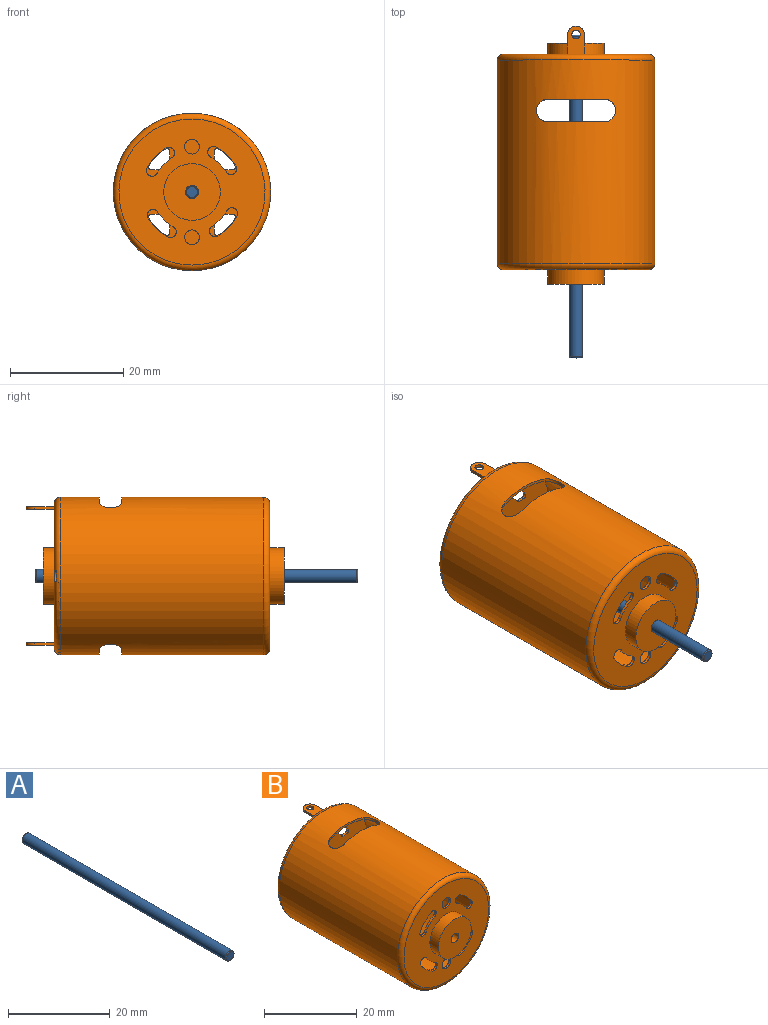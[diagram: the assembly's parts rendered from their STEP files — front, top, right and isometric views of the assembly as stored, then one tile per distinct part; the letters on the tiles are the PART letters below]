
ASSEMBLY  parts=2 mates=1
PART A: 5 faces, bbox 2.5x57x2.5 mm
  f0: cylinder r=1.15mm len=56.6mm, axis (0,1,0), area 409mm2, adj f3,f4
  f1: plane 1.9x1.9mm, normal (0,-1,0), area 2.8mm2, adj f4
  f2: plane 1.9x1.9mm, normal (0,1,0), area 2.8mm2, adj f3
  f3: torus R=0.95mm, axis (0,-1,0), area 2.1mm2, adj f0,f2
  f4: torus R=0.95mm, axis (0,-1,0), area 2.1mm2, adj f0,f1
PART B: 92 faces, bbox 30.1x45.6x30.1 mm
  f0: plane 25.8x25.72mm, normal (0,1,0), area 404mm2, adj f12,f22,f23,f24,f26,f27,f28,f30
  f1: plane 25.8x25.8mm, normal (0,-1,0), area 386.1mm2, adj f4,f5,f10,f62,f63,f64,f65,f66
  f2: plane 26.8x26.8mm, normal (0,1,0), area 501.8mm2, adj f4,f5,f7,f9,f62,f63,f64,f65
  f3: cylinder r=13.9mm len=36mm, axis (0,-1,0), area 3034.5mm2, adj f14,f15,f16,f17,f18,f19,f20,f21
  f4: cylinder r=1.3mm len=2.6mm, axis (0,-1,0), area 4.1mm2, adj f1,f2
  f5: cylinder r=1.3mm len=2.6mm, axis (0,-1,0), area 4.1mm2, adj f1,f2
  f6: plane 26.8x26.8mm, normal (0,-1,0), area 527.4mm2, adj f7,f8,f30,f31,f32,f33,f34,f35
  f7: cylinder r=13.4mm len=37mm, axis (0,-1,0), area 3005.2mm2, adj f2,f6,f14,f15,f16,f17,f18,f19
  f8: cylinder r=1.15mm len=2.5mm, axis (0,-1,0), area 18.1mm2, adj f6,f13
  f9: cylinder r=1.15mm len=3.1mm, axis (0,-1,0), area 22.4mm2, adj f2,f11
  f10: cylinder r=5mm len=10mm, axis (0,1,0), area 81.7mm2, adj f1,f11
  f11: plane 10x10mm, normal (0,-1,0), area 74.4mm2, adj f9,f10
  f12: cylinder r=5mm len=10mm, axis (0,-1,0), area 62.8mm2, adj f0,f13
  f13: plane 10x10mm, normal (0,1,0), area 74.4mm2, adj f8,f12
  f14: plane 10x1.47mm, normal (0,1,0), area 5.1mm2, adj f3,f7,f15,f17
  f15: cylinder r=2mm len=4mm, axis (0,0,1), area 3.5mm2, adj f3,f7,f14,f16
  f16: plane 10x1.47mm, normal (0,-1,0), area 5.1mm2, adj f3,f7,f15,f17
  f17: cylinder r=2mm len=4mm, axis (0,0,1), area 3.5mm2, adj f3,f7,f14,f16
  f18: cylinder r=2mm len=4mm, axis (0,0,1), area 3.5mm2, adj f3,f7,f19,f21
  f19: plane 10x1.47mm, normal (0,-1,0), area 5.1mm2, adj f3,f7,f18,f20
  f20: cylinder r=2mm len=4mm, axis (0,0,1), area 3.5mm2, adj f3,f7,f19,f21
  f21: plane 10x1.47mm, normal (0,1,0), area 5.1mm2, adj f3,f7,f18,f20
  f22: cylinder r=1mm len=2mm, axis (0,1,0), area 0.9mm2, adj f0,f23,f24,f25
  f23: plane 1.08x0.31mm, normal (0,0,-1), area 0.3mm2, adj f0,f22,f25,f79
  f24: plane 1.08x0.31mm, normal (0,0,1), area 0.3mm2, adj f0,f22,f25,f79
  f25: plane 2.11x2mm, normal (0,1,0), area 3.8mm2, adj f22,f23,f24,f79
  f26: plane 1.08x0.31mm, normal (0,0,-1), area 0.3mm2, adj f0,f27,f29,f79
  f27: cylinder r=1mm len=2mm, axis (0,1,0), area 0.9mm2, adj f0,f26,f28,f29
  f28: plane 1.08x0.31mm, normal (0,0,1), area 0.3mm2, adj f0,f27,f29,f79
  f29: plane 2.11x2mm, normal (0,1,0), area 3.8mm2, adj f26,f27,f28,f79
  f30: cylinder r=8.9mm len=2.92mm, axis (0,1,0), area 2.1mm2, adj f0,f6,f34,f35
  f31: plane 1.21x0.5mm, normal (1,0,0), area 0.6mm2, adj f0,f6,f34,f36
  f32: plane 1.21x0.5mm, normal (0,0,1), area 0.6mm2, adj f0,f6,f35,f37
  f33: cylinder r=6.9mm len=1.45mm, axis (0,1,0), area 1mm2, adj f0,f6,f36,f37
  f34: cylinder r=0.5mm len=0.76mm, axis (0,1,0), area 0.5mm2, adj f0,f6,f30,f31
  f35: cylinder r=0.5mm len=0.76mm, axis (0,1,0), area 0.5mm2, adj f0,f6,f30,f32
  f36: cylinder r=0.5mm len=0.5mm, axis (0,1,0), area 0.2mm2, adj f0,f6,f31,f33
  f37: cylinder r=0.5mm len=0.5mm, axis (0,1,0), area 0.2mm2, adj f0,f6,f32,f33
  f38: cylinder r=8.9mm len=2.92mm, axis (0,1,0), area 2.1mm2, adj f0,f6,f42,f43
  f39: plane 1.21x0.5mm, normal (0,0,-1), area 0.6mm2, adj f0,f6,f42,f44
  f40: plane 1.21x0.5mm, normal (1,0,0), area 0.6mm2, adj f0,f6,f43,f45
  f41: cylinder r=6.9mm len=1.45mm, axis (0,1,0), area 1mm2, adj f0,f6,f44,f45
  f42: cylinder r=0.5mm len=0.76mm, axis (0,1,0), area 0.5mm2, adj f0,f6,f38,f39
  f43: cylinder r=0.5mm len=0.76mm, axis (0,1,0), area 0.5mm2, adj f0,f6,f38,f40
  f44: cylinder r=0.5mm len=0.5mm, axis (0,1,0), area 0.2mm2, adj f0,f6,f39,f41
  f45: cylinder r=0.5mm len=0.5mm, axis (0,1,0), area 0.2mm2, adj f0,f6,f40,f41
  f46: cylinder r=8.9mm len=2.92mm, axis (0,1,0), area 2.1mm2, adj f0,f6,f50,f51
  f47: plane 1.21x0.5mm, normal (-1,0,0), area 0.6mm2, adj f0,f6,f50,f52
  f48: plane 1.21x0.5mm, normal (0,0,-1), area 0.6mm2, adj f0,f6,f51,f53
  f49: cylinder r=6.9mm len=1.45mm, axis (0,1,0), area 1mm2, adj f0,f6,f52,f53
  f50: cylinder r=0.5mm len=0.76mm, axis (0,1,0), area 0.5mm2, adj f0,f6,f46,f47
  f51: cylinder r=0.5mm len=0.76mm, axis (0,1,0), area 0.5mm2, adj f0,f6,f46,f48
  f52: cylinder r=0.5mm len=0.5mm, axis (0,1,0), area 0.2mm2, adj f0,f6,f47,f49
  f53: cylinder r=0.5mm len=0.5mm, axis (0,1,0), area 0.2mm2, adj f0,f6,f48,f49
  f54: cylinder r=8.9mm len=2.92mm, axis (0,1,0), area 2.1mm2, adj f0,f6,f58,f59
  f55: plane 1.21x0.5mm, normal (0,0,1), area 0.6mm2, adj f0,f6,f58,f60
  f56: plane 1.21x0.5mm, normal (-1,0,0), area 0.6mm2, adj f0,f6,f59,f61
  f57: cylinder r=6.9mm len=1.45mm, axis (0,1,0), area 1mm2, adj f0,f6,f60,f61
  f58: cylinder r=0.5mm len=0.76mm, axis (0,1,0), area 0.5mm2, adj f0,f6,f54,f55
  f59: cylinder r=0.5mm len=0.76mm, axis (0,1,0), area 0.5mm2, adj f0,f6,f54,f56
  f60: cylinder r=0.5mm len=0.5mm, axis (0,1,0), area 0.2mm2, adj f0,f6,f55,f57
  f61: cylinder r=0.5mm len=0.5mm, axis (0,1,0), area 0.2mm2, adj f0,f6,f56,f57
  f62: cylinder r=7mm len=2.72mm, axis (0,-1,0), area 1.9mm2, adj f1,f2,f63,f64
  f63: cylinder r=1mm len=1.86mm, axis (0,-1,0), area 1.6mm2, adj f1,f2,f62,f65
  f64: cylinder r=1mm len=1.88mm, axis (0,-1,0), area 1.6mm2, adj f1,f2,f62,f65
  f65: cylinder r=9mm len=3.5mm, axis (0,-1,0), area 2.5mm2, adj f1,f2,f63,f64
  f66: cylinder r=7mm len=2.72mm, axis (0,-1,0), area 1.9mm2, adj f1,f2,f67,f68
  f67: cylinder r=1mm len=1.86mm, axis (0,-1,0), area 1.6mm2, adj f1,f2,f66,f69
  f68: cylinder r=1mm len=1.88mm, axis (0,-1,0), area 1.6mm2, adj f1,f2,f66,f69
  f69: cylinder r=9mm len=3.5mm, axis (0,-1,0), area 2.5mm2, adj f1,f2,f67,f68
  f70: cylinder r=7mm len=2.72mm, axis (0,-1,0), area 1.9mm2, adj f1,f2,f71,f72
  f71: cylinder r=1mm len=1.86mm, axis (0,-1,0), area 1.6mm2, adj f1,f2,f70,f73
  f72: cylinder r=1mm len=1.88mm, axis (0,-1,0), area 1.6mm2, adj f1,f2,f70,f73
  f73: cylinder r=9mm len=3.5mm, axis (0,-1,0), area 2.5mm2, adj f1,f2,f71,f72
  f74: cylinder r=7mm len=2.72mm, axis (0,-1,0), area 1.9mm2, adj f1,f2,f75,f76
  f75: cylinder r=1mm len=1.86mm, axis (0,-1,0), area 1.6mm2, adj f1,f2,f74,f77
  f76: cylinder r=1mm len=1.88mm, axis (0,-1,0), area 1.6mm2, adj f1,f2,f74,f77
  f77: cylinder r=9mm len=3.5mm, axis (0,-1,0), area 2.5mm2, adj f1,f2,f75,f76
  f78: torus R=12.9mm, axis (0,-1,0), area 133.6mm2, adj f1,f3
  f79: torus R=12.9mm, axis (0,-1,0), area 130.4mm2, adj f0,f3,f23,f24,f25,f26,f28,f29
  f80: plane 3.5x0.5mm, normal (-1,0,0), area 1.8mm2, adj f0,f81,f83,f89
  f81: plane 5x3mm, normal (0,0,1), area 12.3mm2, adj f0,f80,f82,f89,f91
  f82: plane 3.5x0.5mm, normal (1,0,0), area 1.8mm2, adj f0,f81,f83,f89
  f83: plane 5x3mm, normal (0,0,-1), area 12.3mm2, adj f0,f80,f82,f89,f91
  f84: plane 5x3mm, normal (0,0,-1), area 12.3mm2, adj f0,f85,f87,f88,f90
  f85: plane 3.5x0.5mm, normal (-1,0,0), area 1.8mm2, adj f0,f84,f86,f88
  f86: plane 5x3mm, normal (0,0,1), area 12.3mm2, adj f0,f85,f87,f88,f90
  f87: plane 3.5x0.5mm, normal (1,0,0), area 1.8mm2, adj f0,f84,f86,f88
  f88: cylinder r=1.5mm len=3mm, axis (0,0,1), area 2.4mm2, adj f84,f85,f86,f87
  f89: cylinder r=1.5mm len=3mm, axis (0,0,-1), area 2.4mm2, adj f80,f81,f82,f83
  f90: cylinder r=0.75mm len=1.5mm, axis (0,0,1), area 2.4mm2, adj f84,f86
  f91: cylinder r=0.75mm len=1.5mm, axis (0,0,1), area 2.4mm2, adj f81,f83
PLACE A t=(-1.66,-14.64,0.03)mm
PLACE B t=(-1.66,-14.64,0.03)mm fixed
MATE revolute A.f0 <-> B.f3  axis (0,-1,0) through (-1.66,-30.24,0.03)mm
